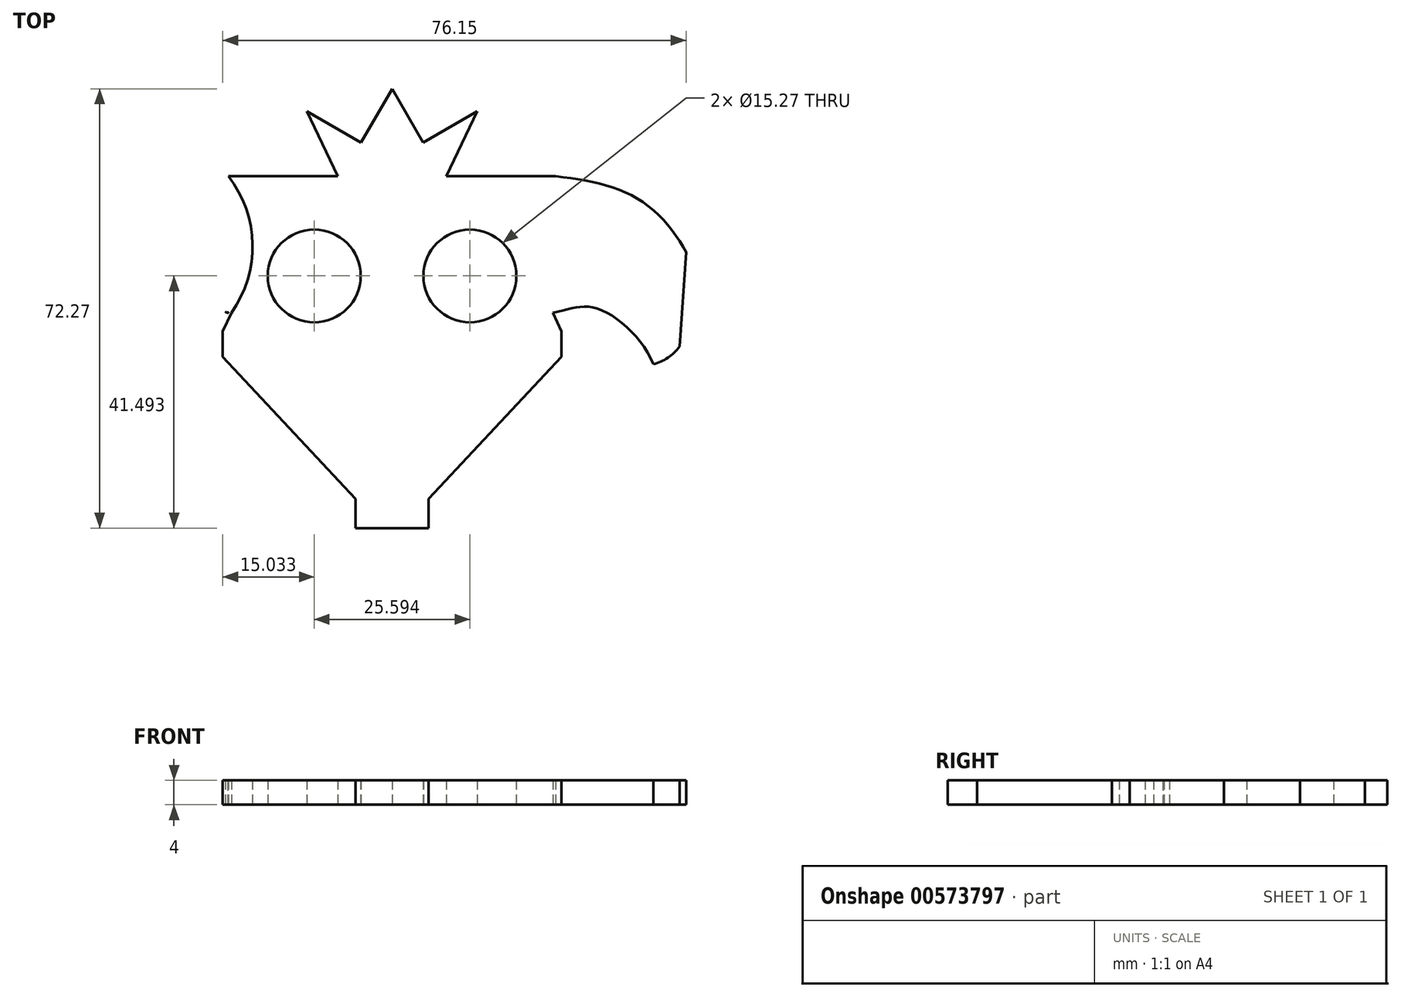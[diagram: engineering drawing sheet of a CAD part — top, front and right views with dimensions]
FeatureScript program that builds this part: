
annotation { "Feature Type Name" : "Feature", "Feature Type Description" : "" }
export const myFeature = defineFeature(function(context is Context, id is Id, definition is map)
    precondition{}
    {
        {
            var Q0;
            Q0=qCreatedBy(makeId("Top.planeOp"),FACE);
            var sketch = newSketch(context, id + "F0", { "sketchPlane" : qUnion([Q0])});
            skLineSegment(sketch, "E0", {"start": v(5.98, -54.31) * mm, "end": v(5.98, -49.5) * mm});
            skLineSegment(sketch, "E1", {"start": v(-7.02, -49.5) * mm, "end": v(-5.98, -49.5) * mm});
            skLineSegment(sketch, "E2", {"start": v(5.98, -49.5) * mm, "end": v(27.83, -26.13) * mm});
            skLineSegment(sketch, "E3", {"start": v(27.83, -26.13) * mm, "end": v(27.83, -21.9) * mm});
            skArc(sketch, "E4", {"start": v(-26.97, -18.88) * mm, "mid": v(-26.94, -18.83) * mm, "end": v(-26.9, -18.78) * mm});
            skLineSegment(sketch, "E5", {"start": v(42.94, -27.33) * mm, "end": v(42.94, -27.33) * mm});
            skLineSegment(sketch, "E6", {"start": v(27.83, -21.9) * mm, "end": v(26.41, -18.88) * mm});
            skFitSpline(sketch, "E7", {"points": [v(-41.09, -27.12) * mm, v(-40.82, -26.56) * mm, v(-35.16, -17.74) * mm, v(-26.97, -18.88) * mm, v(-36.75, -13.5) * mm], "startDerivative": vector(-4.5, -8.5) * mm, "endDerivative": vector(-49.82, 22.25) * mm});
            skLineSegment(sketch, "E8.trimOffspring", {"start": v(-40.82, -26.56) * mm, "end": v(-40.82, -26.56) * mm});
            skLineSegment(sketch, "E9", {"start": v(-27.4, -18.77) * mm, "end": v(-26.93, -18.83) * mm});
            skLineSegment(sketch, "E10", {"start": v(-27.02, -18.88) * mm, "end": v(-26.93, -18.83) * mm});
            skLineSegment(sketch, "E11", {"start": v(-26.93, -18.83) * mm, "end": v(-27.4, -18.77) * mm});
            skFitSpline(sketch, "E12", {"points": [v(26.41, -18.88) * mm, v(33.58, -18.15) * mm, v(42.94, -27.33) * mm], "startDerivative": vector(20.45, 4.2) * mm, "endDerivative": vector(8.45, -22.34) * mm});
            skLineSegment(sketch, "E13", {"start": v(48.32, -8.94) * mm, "end": v(47.25, -24.44) * mm});
            skArc(sketch, "E14.trimOffspring", {"start": v(26.92, 3.57) * mm, "mid": v(22.93, -7.57) * mm, "end": v(26.41, -18.88) * mm});
            skPoint(sketch, "E15.1.internal.orphan", {"position": v(47.25, -26.4) * mm});
            skFitSpline(sketch, "E16", {"points": [v(26.92, 3.57) * mm, v(40.2, 0) * mm, v(48.32, -8.94) * mm], "startDerivative": vector(28.25, -3.32) * mm, "endDerivative": vector(11.09, -21.56) * mm});
            skLineSegment(sketch, "E17", {"start": v(26.92, 3.57) * mm, "end": v(8.9, 3.57) * mm});
            skLineSegment(sketch, "E18", {"start": v(12.5, 13.38) * mm, "end": v(12.57, 13.6) * mm});
            skLineSegment(sketch, "E19", {"start": v(0, 17.96) * mm, "end": v(5.13, 9.11) * mm});
            skLineSegment(sketch, "E20", {"start": v(5.13, 9.11) * mm, "end": v(13.98, 14.25) * mm});
            skLineSegment(sketch, "E21", {"start": v(13.98, 14.25) * mm, "end": v(8.9, 3.57) * mm});
            skArc(sketch, "E22.trimOffspring", {"start": v(-46.43, -25.02) * mm, "mid": v(-46.41, -25.04) * mm, "end": v(-46.4, -25.06) * mm});
            skArc(sketch, "E23", {"start": v(42.94, -27.33) * mm, "mid": v(45.35, -26.26) * mm, "end": v(47.25, -24.44) * mm});
            skPoint(sketch, "E24.start.orphan", {"position": v(39.29, -27.33) * mm});
            skLineSegment(sketch, "E25.MirrorCS", {"start": v(-42.94, -27.33) * mm, "end": v(-42.94, -27.33) * mm});
            skLineSegment(sketch, "E26.MirrorCS", {"start": v(-12.5, 13.38) * mm, "end": v(-12.57, 13.6) * mm});
            skFitSpline(sketch, "E27.MirrorCS", {"points": [v(-26.41, -18.88) * mm, v(-33.58, -18.15) * mm, v(-42.94, -27.33) * mm], "startDerivative": vector(-20.45, 4.2) * mm, "endDerivative": vector(-8.45, -22.34) * mm});
            skPoint(sketch, "E28.MirrorP", {"position": v(-47.25, -26.4) * mm});
            skFitSpline(sketch, "E29.MirrorCS", {"points": [v(-26.92, 3.57) * mm, v(-40.2, 0) * mm, v(-48.32, -8.94) * mm], "startDerivative": vector(-28.25, -3.32) * mm, "endDerivative": vector(-11.09, -21.56) * mm});
            skPoint(sketch, "E30.start.orphan", {"position": v(-14.33, 13.6) * mm});
            skPoint(sketch, "E31.MirrorCS.start.orphan", {"position": v(-5.98, -54.31) * mm});
            skPoint(sketch, "E32.MirrorCS.start.orphan", {"position": v(-5.98, -49.5) * mm});
            skPoint(sketch, "E33.MirrorCS.start.orphan", {"position": v(-27.83, -26.13) * mm});
            skPoint(sketch, "E34.MirrorCS.start.orphan", {"position": v(-27.83, -21.9) * mm});
            skLineSegment(sketch, "E35", {"start": v(5, -12.82) * mm, "end": v(5.16, -12.82) * mm});
            skCircle(sketch, "E36", {"center": v(12.8, -12.82) * mm, "radius": 7.64 * mm});
            skPoint(sketch, "E37.start.orphan", {"position": v(-5.13, 9.11) * mm});
            skPoint(sketch, "E38.MirrorCS.start.orphan", {"position": v(0, 17.96) * mm});
            skPoint(sketch, "E39.MirrorCS.start.orphan", {"position": v(-13.98, 14.25) * mm});
            skLineSegment(sketch, "E40.trimOffspring", {"start": v(0, 3.57) * mm, "end": v(26.92, 3.57) * mm});
            skArc(sketch, "E41.trimOffspring", {"start": v(-28.45, 3.38) * mm, "mid": v(-28.53, 3.47) * mm, "end": v(-28.62, 3.57) * mm});
            skPoint(sketch, "E42.start.orphan", {"position": v(-28.87, -26.13) * mm});
            skPoint(sketch, "E43.1.internal.orphan", {"position": v(-40.55, 0) * mm});
            skLineSegment(sketch, "E44.trimOffspring", {"start": v(0, -49.5) * mm, "end": v(5.98, -49.5) * mm});
            skLineSegment(sketch, "E45.trimOffspring", {"start": v(0, -54.31) * mm, "end": v(5.98, -54.31) * mm});
            skPoint(sketch, "E46.end.orphan", {"position": v(-8.9, 3.57) * mm});
            skPoint(sketch, "E47.MirrorP", {"position": v(5.13, 9.11) * mm});
            skLineSegment(sketch, "E48.MirrorCS", {"start": v(0, -54.31) * mm, "end": v(-5.98, -54.31) * mm});
            skLineSegment(sketch, "E49.MirrorCS", {"start": v(0, -49.5) * mm, "end": v(-5.98, -49.5) * mm});
            skLineSegment(sketch, "E50.MirrorCS", {"start": v(0, 3.57) * mm, "end": v(-26.92, 3.57) * mm});
            skArc(sketch, "E51.MirrorCS", {"start": v(-42.94, -27.33) * mm, "mid": v(-45.35, -26.26) * mm, "end": v(-47.25, -24.44) * mm});
            skLineSegment(sketch, "E52.MirrorCS", {"start": v(-27.83, -21.9) * mm, "end": v(-26.41, -18.88) * mm});
            skLineSegment(sketch, "E53.MirrorCS", {"start": v(-27.83, -26.13) * mm, "end": v(-27.83, -21.9) * mm});
            skCircle(sketch, "E54.MirrorC", {"center": v(-12.8, -12.82) * mm, "radius": 7.64 * mm});
            skLineSegment(sketch, "E55.MirrorCS", {"start": v(-5, -12.82) * mm, "end": v(-5.16, -12.82) * mm});
            skFitSpline(sketch, "E56.MirrorCS", {"points": [v(-26.41, -18.88) * mm, v(-33.58, -18.15) * mm, v(-42.94, -27.33) * mm], "startDerivative": vector(-20.45, 4.2) * mm, "endDerivative": vector(-8.45, -22.34) * mm});
            skLineSegment(sketch, "E57.MirrorCS", {"start": v(-13.98, 14.25) * mm, "end": v(-8.9, 3.57) * mm});
            skArc(sketch, "E58.MirrorCS", {"start": v(-26.92, 3.57) * mm, "mid": v(-22.93, -7.57) * mm, "end": v(-26.41, -18.88) * mm});
            skLineSegment(sketch, "E59.MirrorCS", {"start": v(-48.32, -8.94) * mm, "end": v(-47.25, -24.44) * mm});
            skLineSegment(sketch, "E60.MirrorCS", {"start": v(-5.98, -49.5) * mm, "end": v(-27.83, -26.13) * mm});
            skLineSegment(sketch, "E61.MirrorCS", {"start": v(-5.98, -54.31) * mm, "end": v(-5.98, -49.5) * mm});
            skLineSegment(sketch, "E62.MirrorCS", {"start": v(-5.13, 9.11) * mm, "end": v(-13.98, 14.25) * mm});
            skLineSegment(sketch, "E63.MirrorCS", {"start": v(-26.92, 3.57) * mm, "end": v(-8.9, 3.57) * mm});
            skFitSpline(sketch, "E64.MirrorCS", {"points": [v(-26.92, 3.57) * mm, v(-40.2, 0) * mm, v(-48.32, -8.94) * mm], "startDerivative": vector(-28.25, -3.32) * mm, "endDerivative": vector(-11.09, -21.56) * mm});
            skLineSegment(sketch, "E65", {"start": v(0, 17.96) * mm, "end": v(-5.13, 9.11) * mm});
            skPoint(sketch, "E66.orphan", {"position": v(-23.56, -12.82) * mm});
            skPoint(sketch, "E67.start.orphan", {"position": v(0, 21.41) * mm});
            skSolve(sketch);
        }
        {
            var Q0;
            Q0=makeQuery(id+"F0.imprint","IMPRINT",FACE,{"disambiguationData":[TD([[makeQuery(id+"F0.imprint","IMPRINT",EDGE,{"derivedFrom":sQuery(id+"F0.wireOp",EDGE,"E0")}),1.0]])]});
            var Q1;
            Q1=makeQuery(id+"F0.imprint","IMPRINT",FACE,{"disambiguationData":[TD([[makeQuery(id+"F0.imprint","IMPRINT",EDGE,{"derivedFrom":sQuery(id+"F0.wireOp",EDGE,"E12")}),1.0]])]});
            var Q2;
            {var subQ6=sQuery(id+"F0.wireOp",EDGE,"E19");Q2=makeQuery(id+"F0.imprint","IMPRINT",FACE,{"disambiguationData":[TD([[makeQuery(id+"F0.imprint","IMPRINT",EDGE,{"derivedFrom":subQ6}),-1.0]])]});}
            var Q3;
            {var subQ2=sQuery(id+"F0.wireOp",EDGE,"E51.MirrorCS");Q3=makeQuery(id+"F0.imprint","IMPRINT",FACE,{"disambiguationData":[TD([[makeQuery(id+"F0.imprint","IMPRINT",EDGE,{"derivedFrom":subQ2}),-1.0]])]});}
            var Q4;
            Q4=makeQuery(id+"F0.imprint","IMPRINT",FACE,{"disambiguationData":[TD([[makeQuery(id+"F0.imprint","IMPRINT",EDGE,{"derivedFrom":sQuery(id+"F0.wireOp",EDGE,"E2")}),1.0]])]});
            var Q5;
            {var subQ3=sQuery(id+"F0.wireOp",EDGE,"E11");Q5=makeQuery(id+"F0.imprint","IMPRINT",FACE,{"disambiguationData":[TD([[makeQuery(id+"F0.imprint","IMPRINT",EDGE,{"derivedFrom":subQ3}),-1.0]])]});}
            var Q6;
            {var subQ0=sQuery(id+"F0.wireOp",EDGE,"E7");var subQ1=sQuery(id+"F0.wireOp",EDGE,"E4");var subQ2=makeQuery(id+"F0.imprint","INTERSECT",VERTEX,{"derivedFrom":[subQ1,subQ0]});Q6=makeQuery(id+"F0.imprint","IMPRINT",FACE,{"disambiguationData":[TD([[makeQuery(id+"F0.imprint","IMPRINT",EDGE,{"disambiguationData":[TD([[subQ2,-1.0]])],"derivedFrom":subQ1}),-1.0]])]});}
            var Q7;
            {var subQ0=sQuery(id+"F0.wireOp",EDGE,"E10");Q7=makeQuery(id+"F0.imprint","IMPRINT",FACE,{"disambiguationData":[TD([[makeQuery(id+"F0.imprint","IMPRINT",EDGE,{"derivedFrom":subQ0}),1.0]])]});}
            var Q8;
            {var subQ3=sQuery(id+"F0.wireOp",EDGE,"E10");Q8=makeQuery(id+"F0.imprint","IMPRINT",FACE,{"disambiguationData":[TD([[makeQuery(id+"F0.imprint","IMPRINT",EDGE,{"derivedFrom":subQ3}),-1.0]])]});}
            extrude(context, id + "F1", {"entities" : qUnion([Q0, Q1, Q2, Q3, Q4, Q5, Q6, Q7, Q8]), "depth" : 4 * mm, "offsetDistance" : 25 * mm});
        }
    });
